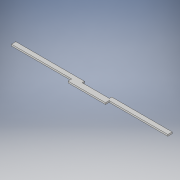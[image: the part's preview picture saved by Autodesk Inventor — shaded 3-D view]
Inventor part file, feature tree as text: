
AUTODESK INVENTOR PART (.ipt)
format: ipt  version: 2017 (Build 210142000, 142)  size: 110,592 bytes
history: native  units: in
note: dims shown in document units (in); Inventor stores cm internally (conversion verified against a paired STEP export)
features: extrude x1, sketch x1
ambient origin geometry x8: Origin, YZ Plane, XZ Plane, XY Plane, X Axis, Y Axis, Z Axis, Center Point
bodies: Solid1 (feature_tree)
feature tree (2):
  extrude  "Extrusion1"  Depth=2.1in
  sketch  "Sketch1"  dims[d0=75.0in d1=2.1in d2=2.1in d3=2.7in d4=0.9in d5=4.1in d6=1.15in d7=18.0in d8=28.125in d9=0.75in d10=0.0in]
